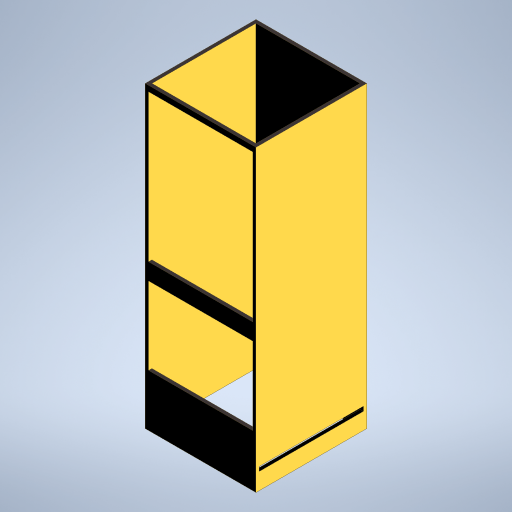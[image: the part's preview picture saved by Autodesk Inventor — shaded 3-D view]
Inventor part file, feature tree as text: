
AUTODESK INVENTOR PART (.ipt)
format: ipt  version: 2024.3 (Build 283343000, 343)  size: 475,648 bytes
history: native  units: mm
features: extrude x3, sketch x3
ambient origin geometry x8: Origin, YZ Plane, XZ Plane, XY Plane, X Axis, Y Axis, Z Axis, Center Point
bodies: Solid1 (feature_tree)
feature tree (6):
  extrude  "Extrusion1"  Depth=100.0mm
  extrude  "Extrusion2"  Depth=3.0mm
  extrude  "Extrusion10"  Depth=94.0mm
  sketch  "Sketch1"  dims[d0=100.0mm d1=100.0mm]
  sketch  "Sketch2"  dims[d2=3.0mm d3=3.0mm]
  sketch  "Sketch10"  dims[d4=270.0mm d5=0.0mm d6=94.0mm d7=3.0mm d8=5.0mm d9=133.0mm d10=70.0mm d11=15.0mm d12=3.0mm d13=10.0mm d14=0.0mm d46=4.0mm d47=10.0mm d48=0.0mm d49=15.0mm]
